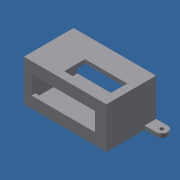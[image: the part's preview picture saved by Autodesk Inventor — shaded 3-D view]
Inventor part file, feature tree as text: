
AUTODESK INVENTOR PART (.ipt)
format: ipt  version: 2021 (Build 250183000, 183)  size: 140,288 bytes
history: native  units: mm
features: extrude x4, sketch x4, other x1
ambient origin geometry x8: Origin, YZ Plane, XZ Plane, XY Plane, X Axis, Y Axis, Z Axis, Center Point
bodies: Solid1 (feature_tree)
feature tree (9):
  other  "<userpath>\OneDrive\Objet3D\3DPrinter\Parameters.xlsx"
  extrude  "Extrusion1"  Depth=44.0mm
  extrude  "Extrusion2"  Depth=5.0mm
  extrude  "Extrusion4"  Depth=5.0mm
  extrude  "Extrusion5"  Depth=5.0mm TaperAngle=0.0deg
  sketch  "Sketch1"  dims[d0=98.0mm d1=44.0mm]
  sketch  "Sketch2"  dims[d2=5.0mm d3=5.0mm]
  sketch  "Sketch4"  dims[d4=5.0mm d5=5.0mm]
  sketch  "Sketch5"  dims[d6=60.0mm d7=0.0mm d8=5.0mm d9=0.0mm d10=10.0mm d11=15.0mm d12=15.0mm d13=15.0mm d19=27.2mm d20=55.2mm d21=10.0mm d22=10.0mm d23=10.0mm d24=0.0mm d25=15.0mm d26=5.0mm d27=15.0mm d28=5.0mm d29=0.0mm]
